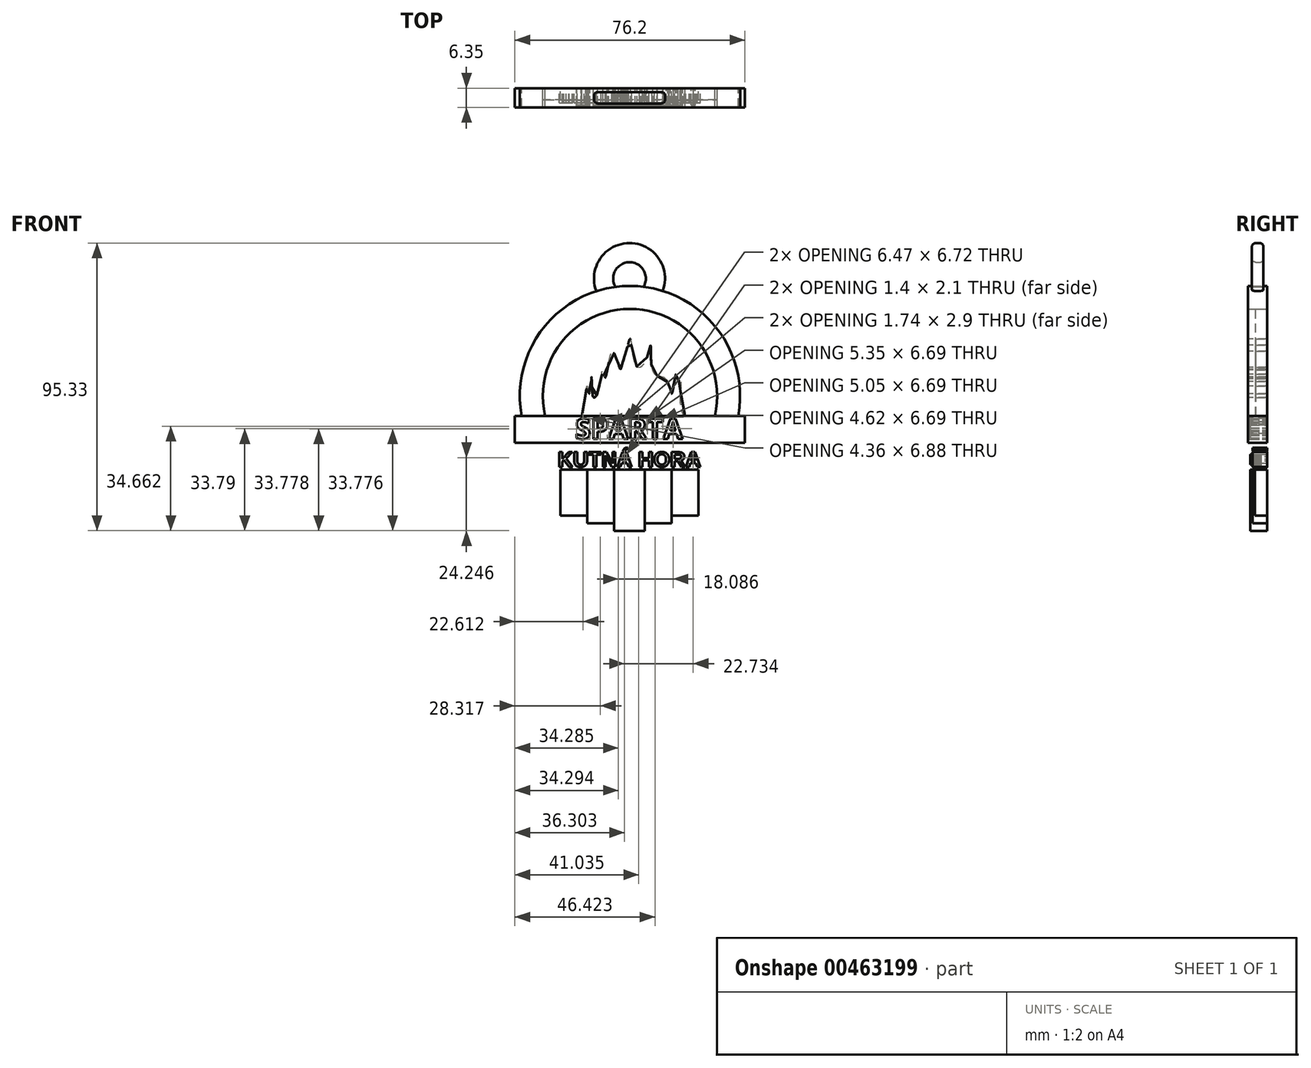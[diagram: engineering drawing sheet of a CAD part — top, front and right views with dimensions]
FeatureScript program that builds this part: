
annotation { "Feature Type Name" : "Feature", "Feature Type Description" : "" }
export const myFeature = defineFeature(function(context is Context, id is Id, definition is map)
    precondition{}
    {
        {
            var Q0;
            Q0=qCreatedBy(makeId("Front.planeOp"),FACE);
            var sketch = newSketch(context, id + "F0", { "sketchPlane" : qUnion([Q0])});
            skLineSegment(sketch, "E0.top", {"start": v(-38.1, 4.44) * mm, "end": v(38.1, 4.44) * mm});
            skLineSegment(sketch, "E0.left", {"start": v(-38.1, -4.45) * mm, "end": v(-38.1, 4.45) * mm});
            skLineSegment(sketch, "E0.right", {"start": v(38.1, -4.45) * mm, "end": v(38.1, 4.44) * mm});
            skPoint(sketch, "E0.middle", {"position": v(0, 0) * mm});
            skArc(sketch, "E1", {"start": v(35.88, 4.45) * mm, "mid": v(0, 47.47) * mm, "end": v(-35.88, 4.45) * mm});
            skArc(sketch, "E2.0", {"start": v(28.1, 4.45) * mm, "mid": v(0, 39.85) * mm, "end": v(-28.1, 4.45) * mm});
            skText(sketch, "E3", { "text": "SPARTA", "fontName": "OpenSans-Bold.ttf"});
            skFitSpline(sketch, "E4", {"points": [v(-15.97, 4.45) * mm, v(-14.16, 14.19) * mm, v(-13.42, 11.8) * mm, v(-12.7, 17.33) * mm, v(-12.11, 10.7) * mm, v(-9.84, 14.49) * mm, v(-9.1, 19.51) * mm, v(-8.28, 17) * mm, v(-5.77, 25.9) * mm, v(-3.17, 19.86) * mm, v(0, 29.94) * mm, v(1.92, 21.13) * mm, v(4.8, 21.9) * mm, v(6.8, 27.86) * mm, v(7.17, 21.03) * mm, v(8.96, 17.72) * mm, v(11.91, 16.57) * mm, v(13.83, 11.8) * mm, v(15.26, 18.2) * mm, v(15.87, 15.77) * mm, v(16.78, 16.68) * mm, v(18.2, 4.45) * mm], "startDerivative": vector(82.82, 240.28) * mm, "endDerivative": vector(118.83, -37.96) * mm});
            skLineSegment(sketch, "E5.bottom", {"start": v(4.93, -31.12) * mm, "end": v(13.82, -31.12) * mm});
            skLineSegment(sketch, "E5.top", {"start": v(4.93, -13.34) * mm, "end": v(13.82, -13.34) * mm});
            skLineSegment(sketch, "E5.left", {"start": v(4.93, -31.11) * mm, "end": v(4.93, -13.33) * mm});
            skLineSegment(sketch, "E5.right", {"start": v(13.82, -31.11) * mm, "end": v(13.82, -13.33) * mm});
            skLineSegment(sketch, "E6.bottom", {"start": v(-5.23, -31.12) * mm, "end": v(-14.12, -31.12) * mm});
            skLineSegment(sketch, "E6.top", {"start": v(-5.23, -13.34) * mm, "end": v(-14.12, -13.34) * mm});
            skLineSegment(sketch, "E6.left", {"start": v(-5.23, -31.11) * mm, "end": v(-5.23, -13.33) * mm});
            skLineSegment(sketch, "E6.right", {"start": v(-14.12, -31.11) * mm, "end": v(-14.12, -13.33) * mm});
            skLineSegment(sketch, "E7.bottom", {"start": v(13.82, -28.58) * mm, "end": v(22.71, -28.58) * mm});
            skLineSegment(sketch, "E7.top", {"start": v(13.82, -13.34) * mm, "end": v(22.71, -13.34) * mm});
            skLineSegment(sketch, "E7.left", {"start": v(13.82, -28.57) * mm, "end": v(13.82, -13.33) * mm});
            skLineSegment(sketch, "E7.right", {"start": v(22.71, -28.57) * mm, "end": v(22.71, -13.33) * mm});
            skLineSegment(sketch, "E8.bottom", {"start": v(-14.12, -28.58) * mm, "end": v(-23, -28.58) * mm});
            skLineSegment(sketch, "E8.top", {"start": v(-14.12, -13.34) * mm, "end": v(-23, -13.34) * mm});
            skLineSegment(sketch, "E8.left", {"start": v(-14.12, -28.57) * mm, "end": v(-14.12, -13.33) * mm});
            skLineSegment(sketch, "E8.right", {"start": v(-23, -28.57) * mm, "end": v(-23, -13.33) * mm});
            skLineSegment(sketch, "E9.bottom", {"start": v(-5.23, -13.34) * mm, "end": v(4.93, -13.34) * mm});
            skLineSegment(sketch, "E9.top", {"start": v(-5.23, -33.66) * mm, "end": v(4.93, -33.66) * mm});
            skLineSegment(sketch, "E9.left", {"start": v(-5.23, -13.33) * mm, "end": v(-5.23, -33.65) * mm});
            skLineSegment(sketch, "E9.right", {"start": v(4.93, -13.33) * mm, "end": v(4.93, -33.65) * mm});
            skLineSegment(sketch, "E10", {"start": v(-38.1, -4.45) * mm, "end": v(38.1, -4.45) * mm});
            skLineSegment(sketch, "E11.bottom", {"start": v(32.08, -4.44) * mm, "end": v(-31.42, -4.45) * mm});
            skLineSegment(sketch, "E11.top", {"start": v(32.08, -13.33) * mm, "end": v(-31.42, -13.33) * mm});
            skLineSegment(sketch, "E11.left", {"start": v(32.08, -4.44) * mm, "end": v(32.08, -13.33) * mm});
            skLineSegment(sketch, "E11.right", {"start": v(-31.42, -4.45) * mm, "end": v(-31.42, -13.33) * mm});
            skText(sketch, "E12", { "text": "KUTNÁ HORA", "fontName": "Arimo-Bold.ttf"});
            skArc(sketch, "E13", {"start": v(4.53, 47.19) * mm, "mid": v(-0.15, 55.33) * mm, "end": v(-4.78, 47.16) * mm});
            skArc(sketch, "E14.0", {"start": v(10, 43.97) * mm, "mid": v(-0.18, 61.68) * mm, "end": v(-10.23, 43.9) * mm});
            const initialGuessF0  = {"E3": [-0.0181, -0.00322, 1, 0, 0.00675], "E12": [-0.02394, -0.01246, 1, 0, 0.00508]};
            skSetInitialGuess(sketch, initialGuessF0);
            skSolve(sketch);
        }
        {
            var Q0;
            {var subQ7=sQuery(id+"F0.wireOp",EDGE,"E2.0");Q0=makeQuery(id+"F0.imprint","IMPRINT",FACE,{"disambiguationData":[TD([[makeQuery(id+"F0.imprint","IMPRINT",EDGE,{"derivedFrom":subQ7}),-1.0]])]});}
            var Q1;
            {var subQ0=sQuery(id+"F0.wireOp",EDGE,"E4");Q1=makeQuery(id+"F0.imprint","IMPRINT",FACE,{"disambiguationData":[TD([[makeQuery(id+"F0.imprint","IMPRINT",EDGE,{"derivedFrom":subQ0}),-1.0]])]});}
            extrude(context, id + "F1", {"entities" : qUnion([Q0, Q1]), "depth" : 6.35 * mm});
        }
        {
            var Q0;
            {var subQ0=sQuery(id+"F0.wireOp",EDGE,"E2.0");Q0=makeQuery(id+"F0.imprint","IMPRINT",FACE,{"disambiguationData":[TD([[makeQuery(id+"F0.imprint","IMPRINT",EDGE,{"derivedFrom":subQ0}),1.0]])]});}
            extrude(context, id + "F2", {"entities" : qUnion([Q0]), "depth" : 3.8 * mm});
        }
        {
            var Q0;
            {var subQ3=sQuery(id+"F0.wireOp",EDGE,"E0.left");Q0=makeQuery(id+"F0.imprint","IMPRINT",FACE,{"disambiguationData":[TD([[makeQuery(id+"F0.imprint","IMPRINT",EDGE,{"derivedFrom":subQ3}),-1.0]])]});}
            var Q1;
            Q1=makeQuery(id+"F0.imprint","IMPRINT",FACE,{"disambiguationData":[TD([[makeQuery(id+"F0.imprint","IMPRINT",EDGE,{"derivedFrom":sQuery(id+"F0.wireOp",EDGE,"E3.sketch_text.stroke-28")}),1.0]])]});
            var Q2;
            Q2=makeQuery(id+"F0.imprint","IMPRINT",FACE,{"disambiguationData":[TD([[makeQuery(id+"F0.imprint","IMPRINT",EDGE,{"derivedFrom":sQuery(id+"F0.wireOp",EDGE,"E3.sketch_text.stroke-52")}),1.0]])]});
            var Q3;
            Q3=makeQuery(id+"F0.imprint","IMPRINT",FACE,{"disambiguationData":[TD([[makeQuery(id+"F0.imprint","IMPRINT",EDGE,{"derivedFrom":sQuery(id+"F0.wireOp",EDGE,"E3.sketch_text.stroke-56")}),1.0]])]});
            var Q4;
            Q4=makeQuery(id+"F0.imprint","IMPRINT",FACE,{"disambiguationData":[TD([[makeQuery(id+"F0.imprint","IMPRINT",EDGE,{"derivedFrom":sQuery(id+"F0.wireOp",EDGE,"E3.sketch_text.stroke-91")}),1.0]])]});
            extrude(context, id + "F3", {"entities" : qUnion([Q0, Q1, Q2, Q3, Q4]), "depth" : 6.35 * mm});
        }
        {
            var Q0;
            Q0=makeQuery(id+"F0.imprint","IMPRINT",FACE,{"disambiguationData":[TD([[makeQuery(id+"F0.imprint","IMPRINT",EDGE,{"derivedFrom":sQuery(id+"F0.wireOp",EDGE,"E3.sketch_text.stroke-0")}),-1.0]])]});
            var Q1;
            Q1=makeQuery(id+"F0.imprint","IMPRINT",FACE,{"disambiguationData":[TD([[makeQuery(id+"F0.imprint","IMPRINT",EDGE,{"derivedFrom":sQuery(id+"F0.wireOp",EDGE,"E3.sketch_text.stroke-28")}),-1.0]])]});
            var Q2;
            Q2=makeQuery(id+"F0.imprint","IMPRINT",FACE,{"disambiguationData":[TD([[makeQuery(id+"F0.imprint","IMPRINT",EDGE,{"derivedFrom":sQuery(id+"F0.wireOp",EDGE,"E3.sketch_text.stroke-44")}),-1.0]])]});
            var Q3;
            Q3=makeQuery(id+"F0.imprint","IMPRINT",FACE,{"disambiguationData":[TD([[makeQuery(id+"F0.imprint","IMPRINT",EDGE,{"derivedFrom":sQuery(id+"F0.wireOp",EDGE,"E3.sketch_text.stroke-56")}),-1.0]])]});
            var Q4;
            Q4=makeQuery(id+"F0.imprint","IMPRINT",FACE,{"disambiguationData":[TD([[makeQuery(id+"F0.imprint","IMPRINT",EDGE,{"derivedFrom":sQuery(id+"F0.wireOp",EDGE,"E3.sketch_text.stroke-75")}),-1.0]])]});
            var Q5;
            Q5=makeQuery(id+"F0.imprint","IMPRINT",FACE,{"disambiguationData":[TD([[makeQuery(id+"F0.imprint","IMPRINT",EDGE,{"derivedFrom":sQuery(id+"F0.wireOp",EDGE,"E3.sketch_text.stroke-83")}),-1.0]])]});
            extrude(context, id + "F4", {"entities" : qUnion([Q0, Q1, Q2, Q3, Q4, Q5]), "depth" : 5.6 * mm});
        }
        {
            var Q0;
            {var subQ0=sQuery(id+"F0.wireOp",EDGE,"E13");Q0=makeQuery(id+"F0.imprint","IMPRINT",FACE,{"disambiguationData":[TD([[makeQuery(id+"F0.imprint","IMPRINT",EDGE,{"derivedFrom":subQ0}),-1.0]])]});}
            extrude(context, id + "F5", {"entities" : qUnion([Q0]), "operationType" : NewBodyOperationType.ADD, "flatOperationType" : FlatOperationType.REMOVE, "offsetDistance" : 25 * mm, "depth" : 5.08 * mm, "hasSecondDirection" : true, "secondDirectionOppositeDirection" : false, "secondDirectionDepth" : 1.27 * mm, "domain" : OperationDomain.MODEL});
        }
        {
            var Q0;
            {var subQ1=sQuery(id+"F0.wireOp",EDGE,"E6.bottom");Q0=makeQuery(id+"F0.imprint","IMPRINT",FACE,{"disambiguationData":[TD([[makeQuery(id+"F0.imprint","IMPRINT",EDGE,{"derivedFrom":subQ1}),-1.0]])]});}
            var Q1;
            {var subQ1=sQuery(id+"F0.wireOp",EDGE,"E5.bottom");Q1=makeQuery(id+"F0.imprint","IMPRINT",FACE,{"disambiguationData":[TD([[makeQuery(id+"F0.imprint","IMPRINT",EDGE,{"derivedFrom":subQ1}),1.0]])]});}
            extrude(context, id + "F6", {"entities" : qUnion([Q0, Q1]), "depth" : 4.83 * mm});
        }
        {
            var Q0;
            Q0=makeQuery(id+"F0.imprint","IMPRINT",FACE,{"disambiguationData":[TD([[makeQuery(id+"F0.imprint","IMPRINT",EDGE,{"derivedFrom":sQuery(id+"F0.wireOp",EDGE,"E11.bottom")}),1.0]])]});
            var Q1;
            Q1=makeQuery(id+"F0.imprint","IMPRINT",FACE,{"disambiguationData":[TD([[makeQuery(id+"F0.imprint","IMPRINT",EDGE,{"derivedFrom":sQuery(id+"F0.wireOp",EDGE,"E12.sketch_text.stroke-54")}),1.0]])]});
            var Q2;
            Q2=makeQuery(id+"F0.imprint","IMPRINT",FACE,{"disambiguationData":[TD([[makeQuery(id+"F0.imprint","IMPRINT",EDGE,{"derivedFrom":sQuery(id+"F0.wireOp",EDGE,"E12.sketch_text.stroke-88")}),1.0]])]});
            var Q3;
            Q3=makeQuery(id+"F0.imprint","IMPRINT",FACE,{"disambiguationData":[TD([[makeQuery(id+"F0.imprint","IMPRINT",EDGE,{"derivedFrom":sQuery(id+"F0.wireOp",EDGE,"E12.sketch_text.stroke-108")}),1.0]])]});
            var Q4;
            Q4=makeQuery(id+"F0.imprint","IMPRINT",FACE,{"disambiguationData":[TD([[makeQuery(id+"F0.imprint","IMPRINT",EDGE,{"derivedFrom":sQuery(id+"F0.wireOp",EDGE,"E12.sketch_text.stroke-122")}),1.0]])]});
            extrude(context, id + "F7", {"entities" : qUnion([Q0, Q1, Q2, Q3, Q4]), "depth" : 5.6 * mm});
        }
        {
            var Q0;
            Q0=makeQuery(id+"F0.imprint","IMPRINT",FACE,{"disambiguationData":[TD([[makeQuery(id+"F0.imprint","IMPRINT",EDGE,{"derivedFrom":sQuery(id+"F0.wireOp",EDGE,"E12.sketch_text.stroke-0")}),-1.0]])]});
            var Q1;
            Q1=makeQuery(id+"F0.imprint","IMPRINT",FACE,{"disambiguationData":[TD([[makeQuery(id+"F0.imprint","IMPRINT",EDGE,{"derivedFrom":sQuery(id+"F0.wireOp",EDGE,"E12.sketch_text.stroke-12")}),-1.0]])]});
            var Q2;
            Q2=makeQuery(id+"F0.imprint","IMPRINT",FACE,{"disambiguationData":[TD([[makeQuery(id+"F0.imprint","IMPRINT",EDGE,{"derivedFrom":sQuery(id+"F0.wireOp",EDGE,"E12.sketch_text.stroke-26")}),-1.0]])]});
            var Q3;
            Q3=makeQuery(id+"F0.imprint","IMPRINT",FACE,{"disambiguationData":[TD([[makeQuery(id+"F0.imprint","IMPRINT",EDGE,{"derivedFrom":sQuery(id+"F0.wireOp",EDGE,"E12.sketch_text.stroke-34")}),-1.0]])]});
            var Q4;
            Q4=makeQuery(id+"F0.imprint","IMPRINT",FACE,{"disambiguationData":[TD([[makeQuery(id+"F0.imprint","IMPRINT",EDGE,{"derivedFrom":sQuery(id+"F0.wireOp",EDGE,"E12.sketch_text.stroke-46")}),-1.0]])]});
            var Q5;
            Q5=makeQuery(id+"F0.imprint","IMPRINT",FACE,{"disambiguationData":[TD([[makeQuery(id+"F0.imprint","IMPRINT",EDGE,{"derivedFrom":sQuery(id+"F0.wireOp",EDGE,"E12.sketch_text.stroke-67")}),-1.0]])]});
            var Q6;
            Q6=makeQuery(id+"F0.imprint","IMPRINT",FACE,{"disambiguationData":[TD([[makeQuery(id+"F0.imprint","IMPRINT",EDGE,{"derivedFrom":sQuery(id+"F0.wireOp",EDGE,"E12.sketch_text.stroke-61")}),-1.0]])]});
            var Q7;
            Q7=makeQuery(id+"F0.imprint","IMPRINT",FACE,{"disambiguationData":[TD([[makeQuery(id+"F0.imprint","IMPRINT",EDGE,{"derivedFrom":sQuery(id+"F0.wireOp",EDGE,"E12.sketch_text.stroke-96")}),-1.0]])]});
            var Q8;
            Q8=makeQuery(id+"F0.imprint","IMPRINT",FACE,{"disambiguationData":[TD([[makeQuery(id+"F0.imprint","IMPRINT",EDGE,{"derivedFrom":sQuery(id+"F0.wireOp",EDGE,"E12.sketch_text.stroke-79")}),-1.0]])]});
            var Q9;
            Q9=makeQuery(id+"F0.imprint","IMPRINT",FACE,{"disambiguationData":[TD([[makeQuery(id+"F0.imprint","IMPRINT",EDGE,{"derivedFrom":sQuery(id+"F0.wireOp",EDGE,"E12.sketch_text.stroke-114")}),-1.0]])]});
            extrude(context, id + "F8", {"entities" : qUnion([Q0, Q1, Q2, Q3, Q4, Q5, Q6, Q7, Q8, Q9]), "depth" : 4.83 * mm});
        }
        {
            var Q0;
            {var subQ6=sQuery(id+"F0.wireOp",EDGE,"E9.top");Q0=makeQuery(id+"F0.imprint","IMPRINT",FACE,{"disambiguationData":[TD([[makeQuery(id+"F0.imprint","IMPRINT",EDGE,{"derivedFrom":subQ6}),1.0]])]});}
            extrude(context, id + "F9", {"entities" : qUnion([Q0]), "depth" : 5.6 * mm});
        }
        {
            var Q0;
            Q0=makeQuery(id+"F0.imprint","IMPRINT",FACE,{"disambiguationData":[TD([[makeQuery(id+"F0.imprint","IMPRINT",EDGE,{"derivedFrom":sQuery(id+"F0.wireOp",EDGE,"E7.bottom")}),1.0]])]});
            var Q1;
            Q1=makeQuery(id+"F0.imprint","IMPRINT",FACE,{"disambiguationData":[TD([[makeQuery(id+"F0.imprint","IMPRINT",EDGE,{"derivedFrom":sQuery(id+"F0.wireOp",EDGE,"E8.bottom")}),-1.0]])]});
            extrude(context, id + "F10", {"entities" : qUnion([Q0, Q1]), "depth" : 4.06 * mm});
        }
        {
            var Q0;
            Q0=makeQuery(id+"F5.opExtrude","CAP_EDGE",EDGE,{"disambiguationData":[OSD([sQuery(id+"F0.wireOp",EDGE,"E14.0")])],"isStart":true});
            var Q1;
            Q1=makeQuery(id+"F5.opExtrude","CAP_EDGE",EDGE,{"disambiguationData":[OSD([sQuery(id+"F0.wireOp",EDGE,"E14.0")])],"isStart":false});
            var Q2;
            Q2=makeQuery(id+"F5.opExtrude","CAP_EDGE",EDGE,{"disambiguationData":[OSD([sQuery(id+"F0.wireOp",EDGE,"E13")])],"isStart":false});
            var Q3;
            Q3=makeQuery(id+"F5.opExtrude","CAP_EDGE",EDGE,{"disambiguationData":[OSD([sQuery(id+"F0.wireOp",EDGE,"E13")])],"isStart":true});
            fillet(context, id + "F11", {"entities" : qUnion([Q0, Q1, Q2, Q3]), "radius" : 1.27 * mm, "tangentPropagation" : true, "allowEdgeOverflow" : false});
        }
    });
